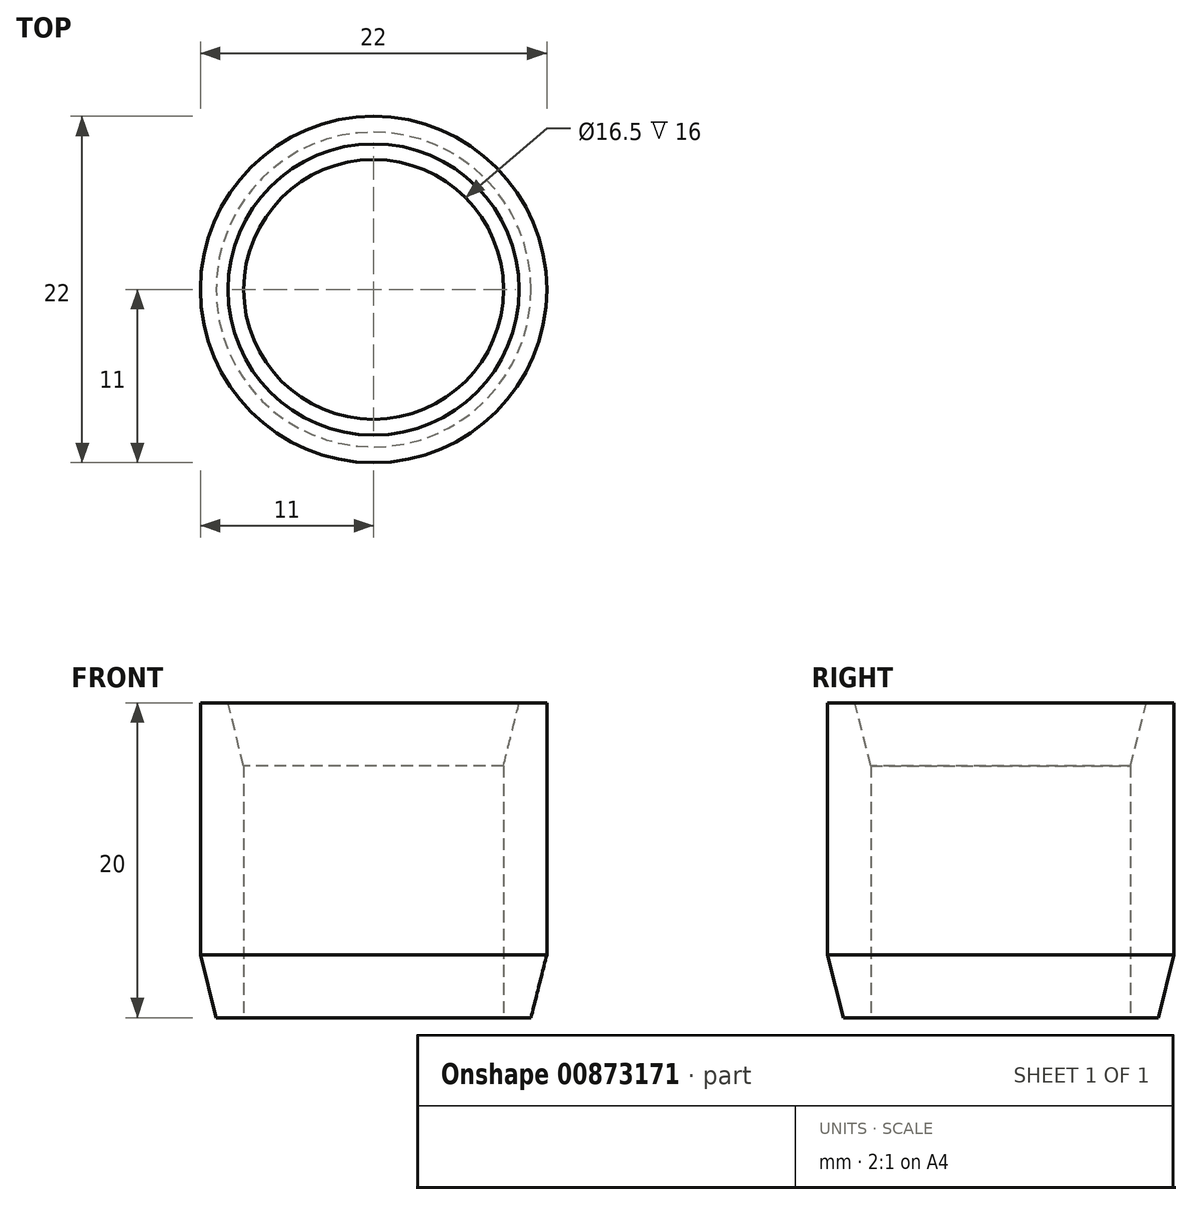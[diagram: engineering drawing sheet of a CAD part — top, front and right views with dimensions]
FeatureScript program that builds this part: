
annotation { "Feature Type Name" : "Feature", "Feature Type Description" : "" }
export const myFeature = defineFeature(function(context is Context, id is Id, definition is map)
    precondition{}
    {
        {
            var Q0;
            Q0=qCreatedBy(makeId("Top.planeOp"),FACE);
            var sketch = newSketch(context, id + "F0", { "sketchPlane" : qUnion([Q0])});
            skCircle(sketch, "E0", {"center": v(0, 0) * mm, "radius": 8.25 * mm});
            skCircle(sketch, "E1", {"center": v(0, 0) * mm, "radius": 11 * mm});
            skSolve(sketch);
        }
        {
            var Q0;
            Q0=makeQuery(id+"F0.imprint","IMPRINT",FACE,{"disambiguationData":[TD([[makeQuery(id+"F0.imprint","IMPRINT",EDGE,{"derivedFrom":sQuery(id+"F0.wireOp",EDGE,"E0")}),-1.0]])]});
            extrude(context, id + "F1", {"entities" : qUnion([Q0]), "depth" : 20 * mm, "offsetDistance" : 25 * mm});
        }
        {
            var Q0;
            Q0=makeQuery(id+"F1.opExtrude","CAP_EDGE",EDGE,{"disambiguationData":[OSD([sQuery(id+"F0.wireOp",EDGE,"E0")])],"isStart":false});
            var Q1;
            Q1=makeQuery(id+"F1.opExtrude","CAP_EDGE",EDGE,{"disambiguationData":[OSD([sQuery(id+"F0.wireOp",EDGE,"E1")])],"isStart":true});
            chamfer(context, id + "F2", {"entities" : qUnion([Q0, Q1]), "chamferType" : ChamferType.TWO_OFFSETS, "width1" : 4 * mm, "oppositeDirection" : false, "width2" : 1 * mm, "tangentPropagation" : true});
        }
    });
